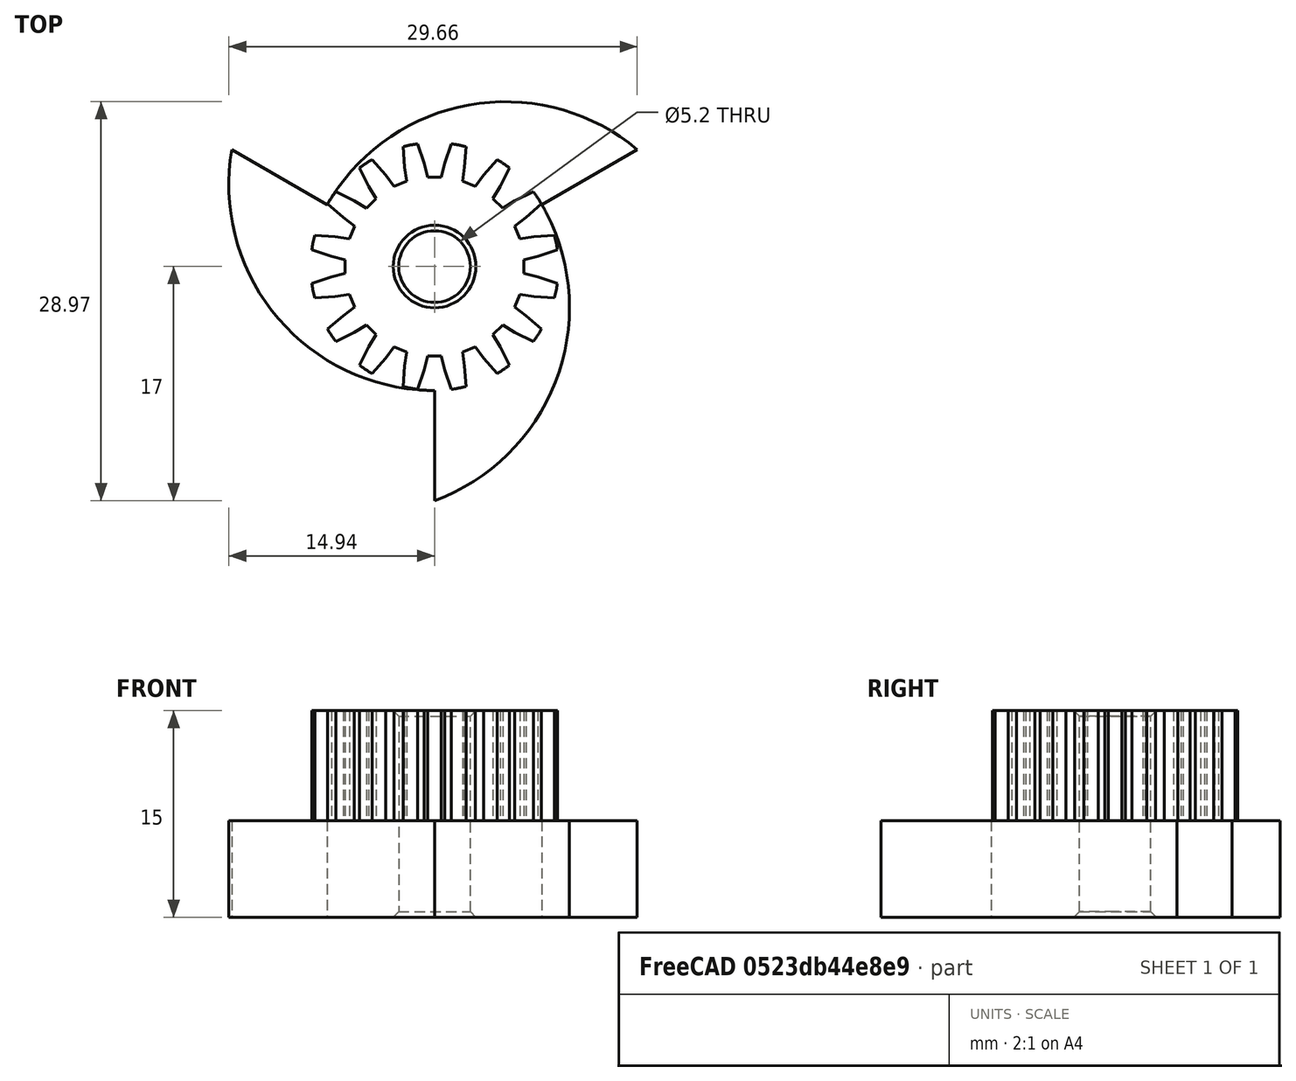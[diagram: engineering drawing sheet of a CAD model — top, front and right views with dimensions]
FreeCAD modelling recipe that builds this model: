
FCSTD DOCUMENT  (FreeCAD 0.18R4 (GitTag))
Label: Stepper_Motor_Wheel_3
License: All rights reserved
LicenseURL: http://en.wikipedia.org/wiki/All_rights_reserved
objects: Sketcher::SketchObject×4, PartDesign::Pocket×3, PartDesign::PolarPattern×2, PartDesign::Revolution×1, PartDesign::Chamfer×1, PartDesign::Body×1, Mesh::Feature×1
note: 16 computed .brp shape members not serialized (recipe doc carries the construction recipe); baked Part::Feature solids carry a one-line shape summary decoded from their .brp

FEATURE [Sketcher::SketchObject] Sketch
  MapMode = 5
  Placement = pos=(0,0,0) rot=(1,0,0;1.5708rad)
  Support = -> [XZ_Plane]
  sketch-geometry (6):
    g0: LineSegment StartX=0 StartY=0 StartZ=0 EndX=17 EndY=0 EndZ=0
    g1: LineSegment StartX=17 StartY=0 StartZ=0 EndX=17 EndY=7 EndZ=0
    g2: LineSegment StartX=17 StartY=7 StartZ=0 EndX=9 EndY=7 EndZ=0
    g3: LineSegment StartX=9 StartY=7 StartZ=0 EndX=9 EndY=15 EndZ=0
    g4: LineSegment StartX=9 StartY=15 StartZ=0 EndX=0 EndY=15 EndZ=0
    g5: LineSegment StartX=0 StartY=15 StartZ=0 EndX=0 EndY=0 EndZ=0
  constraints (17):
    c: Coincident(g-1,g0)
    c: PointOnObject(g0,g-1)
    c: Coincident(g0,g1)
    c: Vertical(g1)
    c: Coincident(g1,g2)
    c: Horizontal(g2)
    c: Coincident(g2,g3)
    c: Vertical(g3)
    c: Coincident(g3,g4)
    c: Horizontal(g4)
    c: PointOnObject(g4,g-2)
    c: DistanceX(g0,g0) = 17
    c: DistanceY(g1,g1) = 7
    c: DistanceY(g3,g3) = 8
    c: DistanceX(g4,g4) = 9
    c: Coincident(g5,g4)
    c: Coincident(g5,g0)
FEATURE [PartDesign::Revolution] Revolution
  Angle = 360
  Axis = (0,2e-16,1)
  Base = (0,0,0)
  Placement = pos=(0,0,0) rot=(1,0,0;1.5708rad)
  Profile = -> Sketch
  ReferenceAxis = -> Sketch [V_Axis]
  Refine = true
  Reversed = true
FEATURE [Sketcher::SketchObject] Sketch001
  ExternalGeometry = -> [Revolution]
  MapMode = 5
  Placement = pos=(0,4.7e-15,7) rot=(0,0,1;3.14159rad)
  Support = -> [Revolution]
  sketch-geometry (6):
    g0: LineSegment StartX=0 StartY=17 StartZ=0 EndX=17 EndY=17 EndZ=0
    g1: LineSegment StartX=0 StartY=17 StartZ=0 EndX=0 EndY=9 EndZ=0
    g2: ArcOfCircle CenterX=0 CenterY=-5.94286 CenterZ=0 NormalX=0 NormalY=0 NormalZ=1 AngleXU=0 Radius=14.9429 StartAngle=6.11121 EndAngle=7.85398
    g3: LineSegment StartX=17 StartY=17 StartZ=0 EndX=17 EndY=-8.5 EndZ=0
    g4: LineSegment StartX=17 StartY=-8.5 StartZ=0 EndX=14.7224 EndY=-8.5 EndZ=0
    g5: LineSegment [constr] StartX=0 StartY=0 StartZ=0 EndX=14.7224 EndY=-8.5 EndZ=0
  constraints (18):
    c: PointOnObject(g0,g-2)
    c: Horizontal(g0)
    c: Coincident(g1,g0)
    c: PointOnObject(g1,g-2)
    c: Coincident(g2,g1)
    c: PointOnObject(g0,g-3)
    c: PointOnObject(g2,g-2)
    c: DistanceY(g1,g1) = 8
    c: Coincident(g0,g3)
    c: Vertical(g3)
    c: Coincident(g3,g4)
    c: Coincident(g4,g2)
    c: Horizontal(g4)
    c: Tangent(g3,g-3)
    c: Coincident(g5,g-1)
    c: PointOnObject(g5,g-3)
    c: Angle(g5,g-2) = 2.0944
    c: Coincident(g5,g2)
FEATURE [PartDesign::Pocket] Pocket
  BaseFeature = -> Revolution
  Length = 7
  Length2 = 100
  Placement = pos=(0,0,0) rot=(1,0,0;1.5708rad)
  Profile = -> Sketch001
  Refine = true
  Type = 0
FEATURE [PartDesign::PolarPattern] PolarPattern
  Angle = 360
  Axis = -> Sketch001 [N_Axis]
  BaseFeature = -> Pocket
  Occurrences = 3
  Originals = -> [Pocket]
  Placement = pos=(0,0,0) rot=(1,0,0;1.5708rad)
  Refine = true
FEATURE [Sketcher::SketchObject] Sketch002
  ExternalGeometry = -> [Revolution]
  MapMode = 5
  Placement = pos=(0,1e-14,15) rot=(0,0,1;3.14159rad)
  Support = -> [Revolution]
  sketch-geometry (6):
    g0: LineSegment StartX=-1.25 StartY=9 StartZ=0 EndX=1.25 EndY=9 EndZ=0
    g1: LineSegment StartX=1.25 StartY=9 StartZ=0 EndX=0.75 EndY=7.5 EndZ=0
    g2: LineSegment StartX=0.75 StartY=7.5 StartZ=0 EndX=0.5 EndY=6.5 EndZ=0
    g3: LineSegment StartX=0.5 StartY=6.5 StartZ=0 EndX=-0.5 EndY=6.5 EndZ=0
    g4: LineSegment StartX=-0.5 StartY=6.5 StartZ=0 EndX=-0.75 EndY=7.5 EndZ=0
    g5: LineSegment StartX=-0.75 StartY=7.5 StartZ=0 EndX=-1.25 EndY=9 EndZ=0
  constraints (15):
    c: Coincident(g0,g1)
    c: Coincident(g1,g2)
    c: Coincident(g2,g3)
    c: Coincident(g3,g4)
    c: Coincident(g4,g5)
    c: Coincident(g5,g0)
    c: Symmetric(g0,g0,g-2)
    c: Symmetric(g3,g2,g-2)
    c: DistanceX(g3,g3) = 1
    c: DistanceX(g4,g1) = 1.5
    c: Symmetric(g4,g1,g-2)
    c: DistanceY(g2,g1) = 1
    c: DistanceY(g2,g0) = 2.5
    c: DistanceX(g0,g0) = 2.5
    c: Tangent(g0,g-3)
FEATURE [PartDesign::Pocket] Pocket001
  BaseFeature = -> PolarPattern
  Length = 8
  Length2 = 100
  Placement = pos=(0,0,0) rot=(1,0,0;1.5708rad)
  Profile = -> Sketch002
  Refine = true
  Type = 0
FEATURE [PartDesign::PolarPattern] PolarPattern001
  Angle = 360
  Axis = -> Sketch002 [N_Axis]
  BaseFeature = -> Pocket001
  Occurrences = 16
  Originals = -> [Pocket001]
  Placement = pos=(0,0,0) rot=(1,0,0;1.5708rad)
  Refine = true
FEATURE [Sketcher::SketchObject] Sketch003
  MapMode = 5
  Placement = pos=(0,1e-14,15) rot=(0,0,1;3.14159rad)
  Support = -> [Revolution]
  sketch-geometry (1):
    g0: Circle CenterX=0 CenterY=0 CenterZ=0 NormalX=0 NormalY=0 NormalZ=1 AngleXU=0 Radius=2.6
  constraints (2):
    c: Coincident(g0,g-1)
    c: Radius(g0) = 2.6
FEATURE [PartDesign::Pocket] Pocket002
  BaseFeature = -> PolarPattern001
  Length = 15
  Length2 = 100
  Placement = pos=(0,0,0) rot=(1,0,0;1.5708rad)
  Profile = -> Sketch003
  Refine = true
  Type = 0
FEATURE [PartDesign::Chamfer] Chamfer
  Base = -> Pocket002 [Face8]
  BaseFeature = -> Pocket002
  Placement = pos=(0,0,0) rot=(1,0,0;1.5708rad)
  Size = 0.4
FEATURE [PartDesign::Body] Body
  Group = -> [Sketch,Revolution,Sketch001,Pocket,PolarPattern,Sketch002,Pocket001,PolarPattern001,Sketch003,Pocket002,Chamfer]
  Origin = -> Origin
  Tip = -> Chamfer
FEATURE [Mesh::Feature] Mesh  label="Body (Meshed)"
